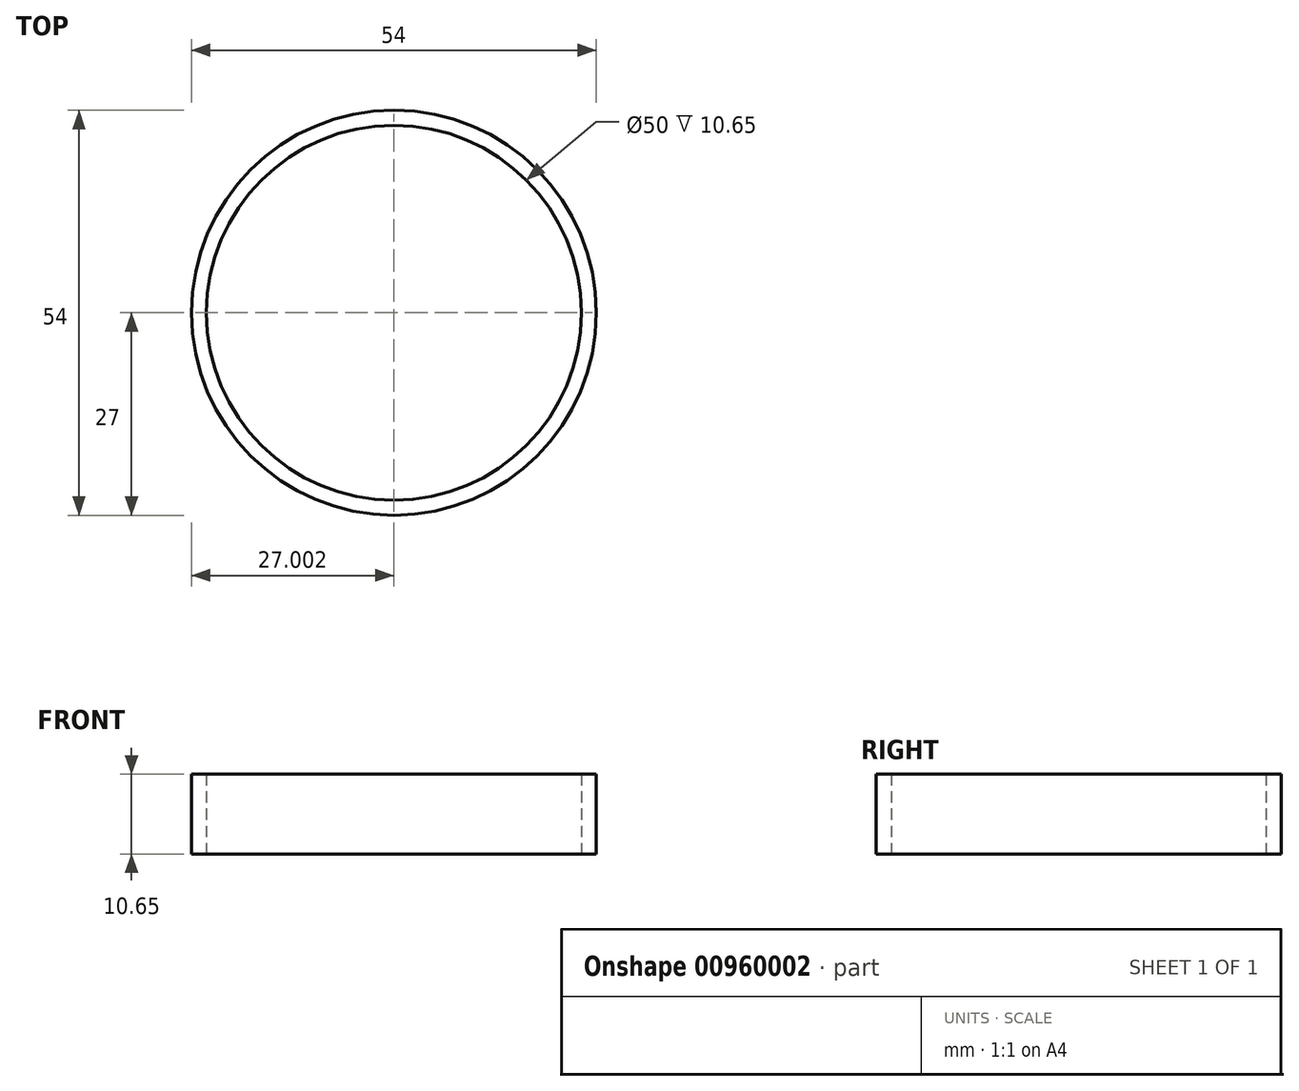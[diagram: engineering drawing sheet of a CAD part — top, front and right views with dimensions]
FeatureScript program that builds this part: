
annotation { "Feature Type Name" : "Feature", "Feature Type Description" : "" }
export const myFeature = defineFeature(function(context is Context, id is Id, definition is map)
    precondition{}
    {
        {
            var Q0;
            Q0=qCreatedBy(makeId("Top.planeOp"),FACE);
            var sketch = newSketch(context, id + "F0", { "sketchPlane" : qUnion([Q0])});
            skCircle(sketch, "E0", {"center": v(3.18, 0) * mm, "radius": 25 * mm});
            skCircle(sketch, "E1.0", {"center": v(3.18, 0) * mm, "radius": 27 * mm});
            skSolve(sketch);
        }
        {
            var Q0;
            Q0=makeQuery(id+"F0.imprint","IMPRINT",FACE,{"disambiguationData":[TD([[makeQuery(id+"F0.imprint","IMPRINT",EDGE,{"derivedFrom":sQuery(id+"F0.wireOp",EDGE,"E0")}),-1.0]])]});
            extrude(context, id + "F1", {"entities" : qUnion([Q0]), "depth" : 10.65 * mm, "offsetDistance" : 25 * mm});
        }
    });
